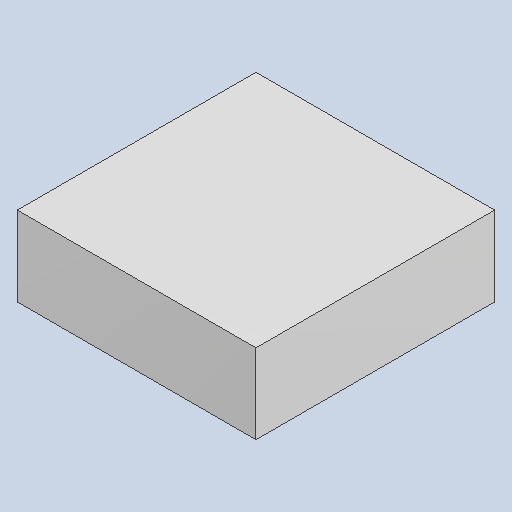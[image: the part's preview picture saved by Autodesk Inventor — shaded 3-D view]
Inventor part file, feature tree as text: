
AUTODESK INVENTOR PART (.ipt)
format: ipt  version: 2023.4 (Build 274418000, 418)  size: 79,872 bytes
history: native  units: mm
features: extrude x1
ambient origin geometry x8: Origin, YZ Plane, XZ Plane, XY Plane, X Axis, Y Axis, Z Axis, Center Point
bodies: Solid1 (feature_tree)
feature tree (1):
  extrude  "Extruded"  [1 undecoded]
note: 1 required parameter value undecoded (feature->parameter linkage not recoverable at this tier; creation-order binding heuristic only, values carry confidence <= 0.55)
